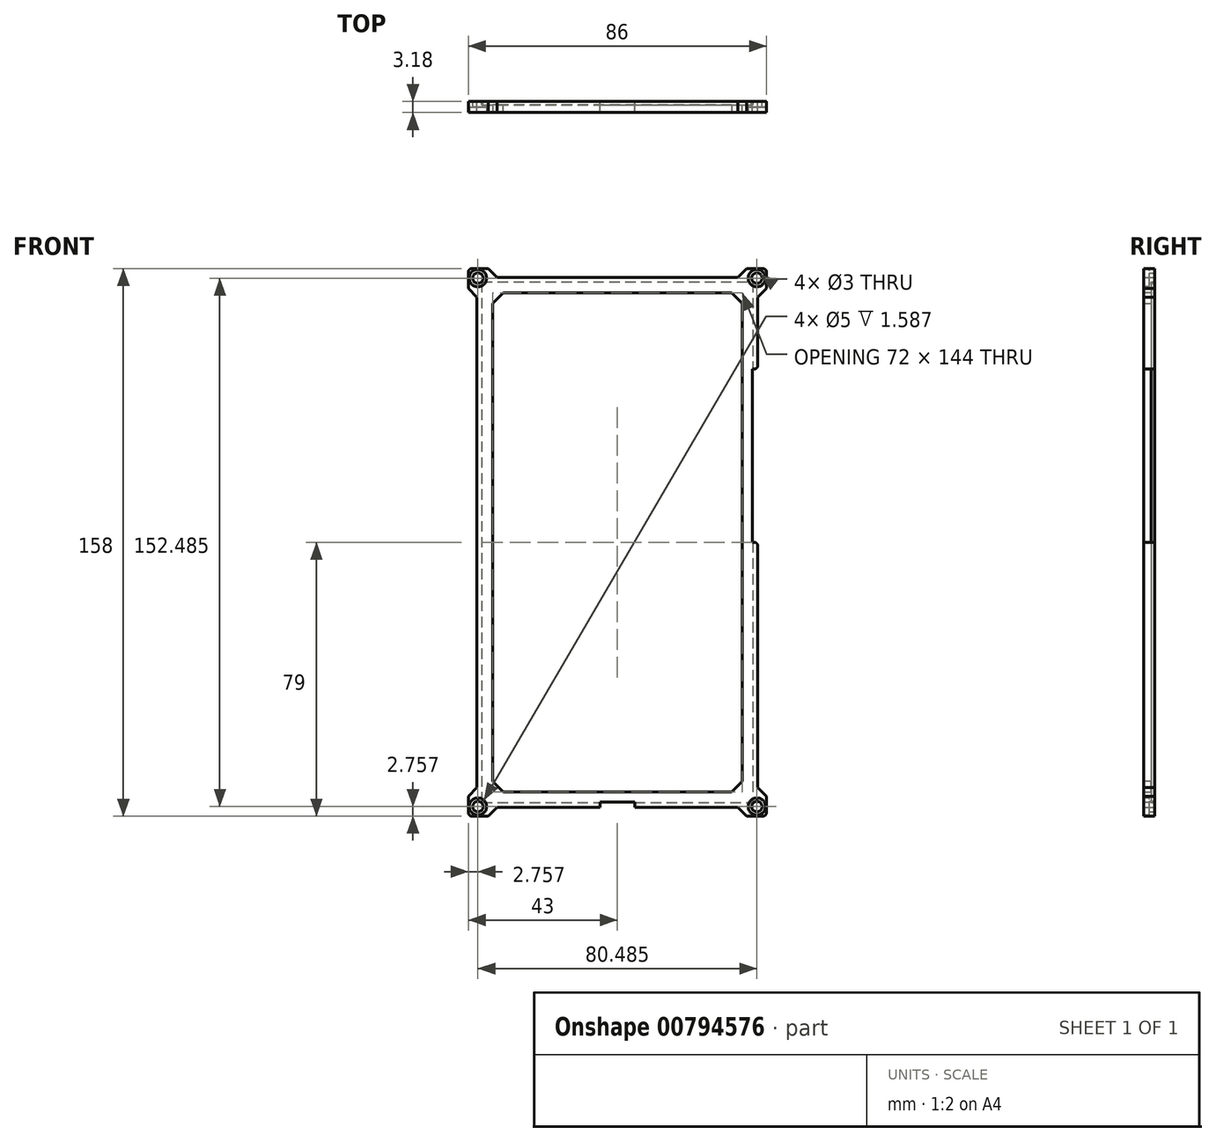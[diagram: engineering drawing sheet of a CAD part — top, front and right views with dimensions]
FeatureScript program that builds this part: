
annotation { "Feature Type Name" : "Feature", "Feature Type Description" : "" }
export const myFeature = defineFeature(function(context is Context, id is Id, definition is map)
    precondition{}
    {
        {
            var Q0;
            Q0=qCreatedBy(makeId("Front.planeOp"),FACE);
            var sketch = newSketch(context, id + "F0", { "sketchPlane" : qUnion([Q0])});
            skLineSegment(sketch, "E0.bottom", {"start": v(39, 75) * mm, "end": v(-39, 75) * mm});
            skLineSegment(sketch, "E0.top", {"start": v(39, -75) * mm, "end": v(-39, -75) * mm});
            skLineSegment(sketch, "E0.left", {"start": v(39, 75) * mm, "end": v(39, -75) * mm});
            skLineSegment(sketch, "E0.right", {"start": v(-39, 75) * mm, "end": v(-39, -75) * mm});
            skPoint(sketch, "E0.middle", {"position": v(0, 0) * mm});
            skSolve(sketch);
        }
        {
            var Q0;
            Q0=qCreatedBy(makeId("Front.planeOp"),FACE);
            var sketch = newSketch(context, id + "F1", { "sketchPlane" : qUnion([Q0])});
            skLineSegment(sketch, "E1.bottom", {"start": v(36, 72) * mm, "end": v(-36, 72) * mm});
            skLineSegment(sketch, "E1.top", {"start": v(36, -72) * mm, "end": v(-36, -72) * mm});
            skLineSegment(sketch, "E1.left", {"start": v(36, 72) * mm, "end": v(36, -72) * mm});
            skLineSegment(sketch, "E1.right", {"start": v(-36, 72) * mm, "end": v(-36, -72) * mm});
            skPoint(sketch, "E1.middle", {"position": v(0, 0) * mm});
            skLineSegment(sketch, "E2.bottom", {"start": v(43, 79) * mm, "end": v(37.24, 79) * mm});
            skLineSegment(sketch, "E2.top", {"start": v(43, -79) * mm, "end": v(37.24, -79) * mm});
            skLineSegment(sketch, "E2.left", {"start": v(43, 79) * mm, "end": v(43, 73.24) * mm});
            skLineSegment(sketch, "E2.right", {"start": v(-43, 79) * mm, "end": v(-43, 73.24) * mm});
            skLineSegment(sketch, "E3", {"start": v(36, 72) * mm, "end": v(43, 79) * mm, "construction": true});
            skLineSegment(sketch, "E4", {"start": v(-36, 72) * mm, "end": v(-43, 79) * mm, "construction": true});
            skLineSegment(sketch, "E5", {"start": v(36, -72) * mm, "end": v(43, -79) * mm, "construction": true});
            skLineSegment(sketch, "E6", {"start": v(-36, -72) * mm, "end": v(-43, -79) * mm, "construction": true});
            skCircle(sketch, "E7", {"center": v(-40.24, 76.24) * mm, "radius": 1.5 * mm});
            skCircle(sketch, "E8", {"center": v(40.24, 76.24) * mm, "radius": 1.5 * mm});
            skCircle(sketch, "E9", {"center": v(40.24, -76.24) * mm, "radius": 1.5 * mm});
            skCircle(sketch, "E10", {"center": v(-40.24, -76.24) * mm, "radius": 1.5 * mm});
            skLineSegment(sketch, "E11.bottom", {"start": v(40.5, 50) * mm, "end": v(39, 50) * mm});
            skLineSegment(sketch, "E11.top", {"start": v(40.5, 0) * mm, "end": v(39, 0) * mm});
            skLineSegment(sketch, "E11.right", {"start": v(39, 50) * mm, "end": v(39, 0) * mm});
            skLineSegment(sketch, "E12.trimOffspring", {"start": v(43, -73.24) * mm, "end": v(43, -79) * mm});
            skLineSegment(sketch, "E13.top", {"start": v(-5, -75) * mm, "end": v(5, -75) * mm});
            skLineSegment(sketch, "E13.left", {"start": v(-5, -76.5) * mm, "end": v(-5, -75) * mm});
            skLineSegment(sketch, "E13.right", {"start": v(5, -76.5) * mm, "end": v(5, -75) * mm});
            skLineSegment(sketch, "E14", {"start": v(0, 0) * mm, "end": v(0, -100.8) * mm, "construction": true});
            skLineSegment(sketch, "E15.trimOffspring", {"start": v(-37.24, -79) * mm, "end": v(-43, -79) * mm});
            skLineSegment(sketch, "E16.top", {"start": v(-37.24, 76.5) * mm, "end": v(37.24, 76.5) * mm});
            skLineSegment(sketch, "E16.left", {"start": v(-37.24, 79) * mm, "end": v(-37.24, 76.5) * mm});
            skLineSegment(sketch, "E16.right", {"start": v(37.24, 79) * mm, "end": v(37.24, 76.5) * mm});
            skLineSegment(sketch, "E17.trimOffspring", {"start": v(-37.24, 79) * mm, "end": v(-43, 79) * mm});
            skLineSegment(sketch, "E18.bottom", {"start": v(43, 73.24) * mm, "end": v(40.5, 73.24) * mm});
            skLineSegment(sketch, "E18.top", {"start": v(43, -73.24) * mm, "end": v(40.5, -73.24) * mm});
            skLineSegment(sketch, "E18.right", {"start": v(40.5, 73.24) * mm, "end": v(40.5, 50) * mm});
            skLineSegment(sketch, "E19.trimOffspring", {"start": v(40.5, 0) * mm, "end": v(40.5, -73.24) * mm});
            skLineSegment(sketch, "E20.top", {"start": v(-37.24, -76.5) * mm, "end": v(-5, -76.5) * mm});
            skLineSegment(sketch, "E20.left", {"start": v(-37.24, -79) * mm, "end": v(-37.24, -76.5) * mm});
            skLineSegment(sketch, "E20.right", {"start": v(37.24, -79) * mm, "end": v(37.24, -76.5) * mm});
            skLineSegment(sketch, "E21.trimOffspring", {"start": v(5, -76.5) * mm, "end": v(37.24, -76.5) * mm});
            skLineSegment(sketch, "E22.bottom", {"start": v(-43, 73.24) * mm, "end": v(-40.5, 73.24) * mm});
            skLineSegment(sketch, "E22.top", {"start": v(-43, -73.24) * mm, "end": v(-40.5, -73.24) * mm});
            skLineSegment(sketch, "E22.right", {"start": v(-40.5, 73.24) * mm, "end": v(-40.5, -73.24) * mm});
            skLineSegment(sketch, "E23.trimOffspring", {"start": v(-43, -73.24) * mm, "end": v(-43, -79) * mm});
            skSolve(sketch);
        }
        {
            var Q0;
            Q0=qSketchRegion(id+"F1",true);
            extrude(context, id + "F2", {"entities" : qUnion([Q0]), "depth" : 3.17 * mm, "offsetDistance" : 25 * mm});
        }
        {
            var Q0;
            Q0=makeQuery(id+"F2.opExtrude","SWEPT_EDGE",EDGE,{"disambiguationData":[OSD([sQuery(id+"F1.wireOp",EDGE,"E1.bottom"),sQuery(id+"F1.wireOp",EDGE,"E1.right")])]});
            var Q1;
            Q1=makeQuery(id+"F2.opExtrude","SWEPT_EDGE",EDGE,{"disambiguationData":[OSD([sQuery(id+"F1.wireOp",EDGE,"E1.bottom"),sQuery(id+"F1.wireOp",EDGE,"E1.left")])]});
            var Q2;
            Q2=makeQuery(id+"F2.opExtrude","SWEPT_EDGE",EDGE,{"disambiguationData":[OSD([sQuery(id+"F1.wireOp",EDGE,"E1.top"),sQuery(id+"F1.wireOp",EDGE,"E1.left")])]});
            var Q3;
            Q3=makeQuery(id+"F2.opExtrude","SWEPT_EDGE",EDGE,{"disambiguationData":[OSD([sQuery(id+"F1.wireOp",EDGE,"E1.top"),sQuery(id+"F1.wireOp",EDGE,"E1.right")])]});
            chamfer(context, id + "F3", {"entities" : qUnion([Q0, Q1, Q2, Q3]), "width" : 3 * mm, "tangentPropagation" : true});
        }
        {
            var Q0;
            Q0=makeQuery(id+"F2.opExtrude","SWEPT_EDGE",EDGE,{"disambiguationData":[OSD([sQuery(id+"F1.wireOp",EDGE,"E16.top"),sQuery(id+"F1.wireOp",EDGE,"E16.left")])]});
            var Q1;
            Q1=makeQuery(id+"F2.opExtrude","SWEPT_EDGE",EDGE,{"disambiguationData":[OSD([sQuery(id+"F1.wireOp",EDGE,"E22.bottom"),sQuery(id+"F1.wireOp",EDGE,"E22.right")])]});
            var Q2;
            Q2=makeQuery(id+"F2.opExtrude","SWEPT_EDGE",EDGE,{"disambiguationData":[OSD([sQuery(id+"F1.wireOp",EDGE,"E18.bottom"),sQuery(id+"F1.wireOp",EDGE,"E18.right")])]});
            var Q3;
            Q3=makeQuery(id+"F2.opExtrude","SWEPT_EDGE",EDGE,{"disambiguationData":[OSD([sQuery(id+"F1.wireOp",EDGE,"E16.top"),sQuery(id+"F1.wireOp",EDGE,"E16.right")])]});
            var Q4;
            Q4=makeQuery(id+"F2.opExtrude","SWEPT_EDGE",EDGE,{"disambiguationData":[OSD([sQuery(id+"F1.wireOp",EDGE,"E20.right"),sQuery(id+"F1.wireOp",EDGE,"E21.trimOffspring")])]});
            var Q5;
            Q5=makeQuery(id+"F2.opExtrude","SWEPT_EDGE",EDGE,{"disambiguationData":[OSD([sQuery(id+"F1.wireOp",EDGE,"E18.top"),sQuery(id+"F1.wireOp",EDGE,"E19.trimOffspring")])]});
            var Q6;
            Q6=makeQuery(id+"F2.opExtrude","SWEPT_EDGE",EDGE,{"disambiguationData":[OSD([sQuery(id+"F1.wireOp",EDGE,"E22.top"),sQuery(id+"F1.wireOp",EDGE,"E22.right")])]});
            var Q7;
            Q7=makeQuery(id+"F2.opExtrude","SWEPT_EDGE",EDGE,{"disambiguationData":[OSD([sQuery(id+"F1.wireOp",EDGE,"E20.top"),sQuery(id+"F1.wireOp",EDGE,"E20.left")])]});
            chamfer(context, id + "F4", {"entities" : qUnion([Q0, Q1, Q2, Q3, Q4, Q5, Q6, Q7]), "width" : 2.5 * mm, "tangentPropagation" : true});
        }
        {
            var Q0;
            Q0=makeQuery(id+"F2.opExtrude","SWEPT_EDGE",EDGE,{"disambiguationData":[OSD([sQuery(id+"F1.wireOp",EDGE,"E2.right"),sQuery(id+"F1.wireOp",EDGE,"E17.trimOffspring")])]});
            var Q1;
            Q1=makeQuery(id+"F2.opExtrude","SWEPT_EDGE",EDGE,{"disambiguationData":[OSD([sQuery(id+"F1.wireOp",EDGE,"E2.bottom"),sQuery(id+"F1.wireOp",EDGE,"E2.left")])]});
            var Q2;
            Q2=makeQuery(id+"F2.opExtrude","SWEPT_EDGE",EDGE,{"disambiguationData":[OSD([sQuery(id+"F1.wireOp",EDGE,"E2.top"),sQuery(id+"F1.wireOp",EDGE,"E12.trimOffspring")])]});
            var Q3;
            Q3=makeQuery(id+"F2.opExtrude","SWEPT_EDGE",EDGE,{"disambiguationData":[OSD([sQuery(id+"F1.wireOp",EDGE,"E15.trimOffspring"),sQuery(id+"F1.wireOp",EDGE,"E23.trimOffspring")])]});
            var Q4;
            Q4=makeQuery(id+"F2.opExtrude","SWEPT_EDGE",EDGE,{"disambiguationData":[OSD([sQuery(id+"F1.wireOp",EDGE,"E11.top"),sQuery(id+"F1.wireOp",EDGE,"E19.trimOffspring")])]});
            var Q5;
            Q5=makeQuery(id+"F2.opExtrude","SWEPT_EDGE",EDGE,{"disambiguationData":[OSD([sQuery(id+"F1.wireOp",EDGE,"E11.bottom"),sQuery(id+"F1.wireOp",EDGE,"E18.right")])]});
            fillet(context, id + "F5", {"entities" : qUnion([Q0, Q1, Q2, Q3, Q4, Q5]), "radius" : 1 * mm, "tangentPropagation" : true, "allowEdgeOverflow" : false});
        }
        {
            var Q0;
            Q0=makeQuery(id+"F2.opExtrude","CAP_FACE",FACE,{"disambiguationData":[OSD([sQuery(id+"F1.wireOp",EDGE,"E1.bottom"),sQuery(id+"F1.wireOp",EDGE,"E1.top"),sQuery(id+"F1.wireOp",EDGE,"E1.left"),sQuery(id+"F1.wireOp",EDGE,"E1.right"),sQuery(id+"F1.wireOp",EDGE,"E2.bottom"),sQuery(id+"F1.wireOp",EDGE,"E2.top"),sQuery(id+"F1.wireOp",EDGE,"E2.left"),sQuery(id+"F1.wireOp",EDGE,"E2.right"),sQuery(id+"F1.wireOp",EDGE,"E7"),sQuery(id+"F1.wireOp",EDGE,"E8"),sQuery(id+"F1.wireOp",EDGE,"E9"),sQuery(id+"F1.wireOp",EDGE,"E10"),sQuery(id+"F1.wireOp",EDGE,"E11.bottom"),sQuery(id+"F1.wireOp",EDGE,"E11.top"),sQuery(id+"F1.wireOp",EDGE,"E11.right"),sQuery(id+"F1.wireOp",EDGE,"E12.trimOffspring"),sQuery(id+"F1.wireOp",EDGE,"E13.top"),sQuery(id+"F1.wireOp",EDGE,"E13.left"),sQuery(id+"F1.wireOp",EDGE,"E13.right"),sQuery(id+"F1.wireOp",EDGE,"E15.trimOffspring"),sQuery(id+"F1.wireOp",EDGE,"E16.top"),sQuery(id+"F1.wireOp",EDGE,"E16.left"),sQuery(id+"F1.wireOp",EDGE,"E16.right"),sQuery(id+"F1.wireOp",EDGE,"E17.trimOffspring"),sQuery(id+"F1.wireOp",EDGE,"E18.bottom"),sQuery(id+"F1.wireOp",EDGE,"E18.top"),sQuery(id+"F1.wireOp",EDGE,"E18.right"),sQuery(id+"F1.wireOp",EDGE,"E19.trimOffspring"),sQuery(id+"F1.wireOp",EDGE,"E20.top"),sQuery(id+"F1.wireOp",EDGE,"E20.left"),sQuery(id+"F1.wireOp",EDGE,"E20.right"),sQuery(id+"F1.wireOp",EDGE,"E21.trimOffspring"),sQuery(id+"F1.wireOp",EDGE,"E22.bottom"),sQuery(id+"F1.wireOp",EDGE,"E22.top"),sQuery(id+"F1.wireOp",EDGE,"E22.right"),sQuery(id+"F1.wireOp",EDGE,"E23.trimOffspring")])],"isStart":false});
            var sketch = newSketch(context, id + "F6", { "sketchPlane" : qUnion([Q0])});
            skCircle(sketch, "E24", {"center": v(-40.24, 76.24) * mm, "radius": 2.5 * mm});
            skCircle(sketch, "E25", {"center": v(40.24, 76.24) * mm, "radius": 2.5 * mm});
            skCircle(sketch, "E26", {"center": v(40.24, -76.24) * mm, "radius": 2.5 * mm});
            skCircle(sketch, "E27", {"center": v(-40.24, -76.24) * mm, "radius": 2.5 * mm});
            skSolve(sketch);
        }
        {
            var Q0;
            Q0 = qSketchRegion(id + "F6", true);
            extrude(context, id + "F7", {"entities" : qUnion([Q0]), "operationType" : NewBodyOperationType.REMOVE, "oppositeDirection" : true, "depth" : 1.59 * mm, "offsetDistance" : 25 * mm});
        }
        {
            var Q0;
            Q0=makeQuery(id+"F0.imprint","IMPRINT",FACE,{"disambiguationData":[TD([[makeQuery(id+"F0.imprint","IMPRINT",EDGE,{"derivedFrom":sQuery(id+"F0.wireOp",EDGE,"E0.bottom")}),1.0]])]});
            var sketch = newSketch(context, id + "F8", { "sketchPlane" : qUnion([Q0])});
            skLineSegment(sketch, "E28.bottom", {"start": v(-39.12, 75.13) * mm, "end": v(39.13, 75.13) * mm});
            skLineSegment(sketch, "E28.top", {"start": v(-39.13, -75.12) * mm, "end": v(39.12, -75.12) * mm});
            skLineSegment(sketch, "E28.left", {"start": v(-39.12, 75.13) * mm, "end": v(-39.13, -75.12) * mm});
            skLineSegment(sketch, "E28.right", {"start": v(39.13, 75.13) * mm, "end": v(39.12, -75.12) * mm});
            skPoint(sketch, "E28.middle", {"position": v(0, 0) * mm});
            skSolve(sketch);
        }
        {
            var Q0;
            Q0 = qSketchRegion(id + "F8", true);
            extrude(context, id + "F9", {"entities" : qUnion([Q0]), "operationType" : NewBodyOperationType.REMOVE, "depth" : 1 * mm, "offsetDistance" : 25 * mm});
        }
    });
